# Revit family: Plumbing_Fixtures-Oasis-Drinking_Fountain_Barrier_Free-Combo-Single-PGEBF-SAN
name_source: partatom
category: Plumbing Fixtures
units: mm (PartAtom-declared; Revit-internal decimal feet)

## family parameters
Cut with Voids When Loaded = No
Host = Face
OmniClass Number = 23.65.70.14.11
OmniClass Title = Drinking Fountains/Coolers
Part Type = Normal
Room Calculation Point = No
Round Connector Dimension = Use Diameter
Shared = No

## types (1)
- PGEBF-SAN
    Accessory Material = Plastic - Oasis International - Gray
    Assembly Code = D2010800
    CW Connection = Yes
    Cabinet Finish = Metal - Oasis International - Steel Painted Sandstone
    Chilling Option = Non-Refrigerated Fountain
    Cold Water Connection Diameter = 0"
    Default Elevation = 1' - 1 9/32"
    Depth = 1' - 6 5/8"
    Description = Non-Refrigerated Fountain
    Filter Option = Option to add filtration
    Finish = Metal - Oasis International - Brushed Stainless Steel
    Flow Rate = 8 GPH
    Frequency = 60 Hz
    Full Load Current = 0 A
    HW Connection = No
    Height = 3' - 1 13/16"
    Instruction Sheet Link = https://www.oasiscoolers.com
    Keynote = 22 40 00.A1
    Load Classification = Power
    Manufacturer = OASIS International
    Manufacturer Fax Number = 1-(614) 322-2529
    Model = PGEBF 507034
    Product Documentation Link = https://www.oasiscoolers.com
    Product Name = Versacooler II W/ Electronic Bottle Filler Versafiller Stainless Steel Alcove, Non-Refrigerated
    Product Page URL = https://www.oasiscoolers.com
    Rated Watts = 11 W
    Screen = Screen – Oasis International - Display - Black
    URL = https://www.oasiscoolers.com
    Vent Connection = No
    Version = 2021 - v1.0a
    Voltage = 115 V
    Voltage Comment = 115 Volts, 60 Hz
    Warranty URL = https://www.oasiscoolers.com
    Waste Connection = Yes
    Waste Water Connection Diameter = 0' - 1 1/4"
    Water Pressure = 60.00 psi
    Water Pressure Range = 20 - 100 PSI
    Weight = 31.00 lb
    Width = 1' - 5 5/8"

## geometry (parser evidence)
native form markers: Sweep x1
no freeform markers — native parametric forms only
